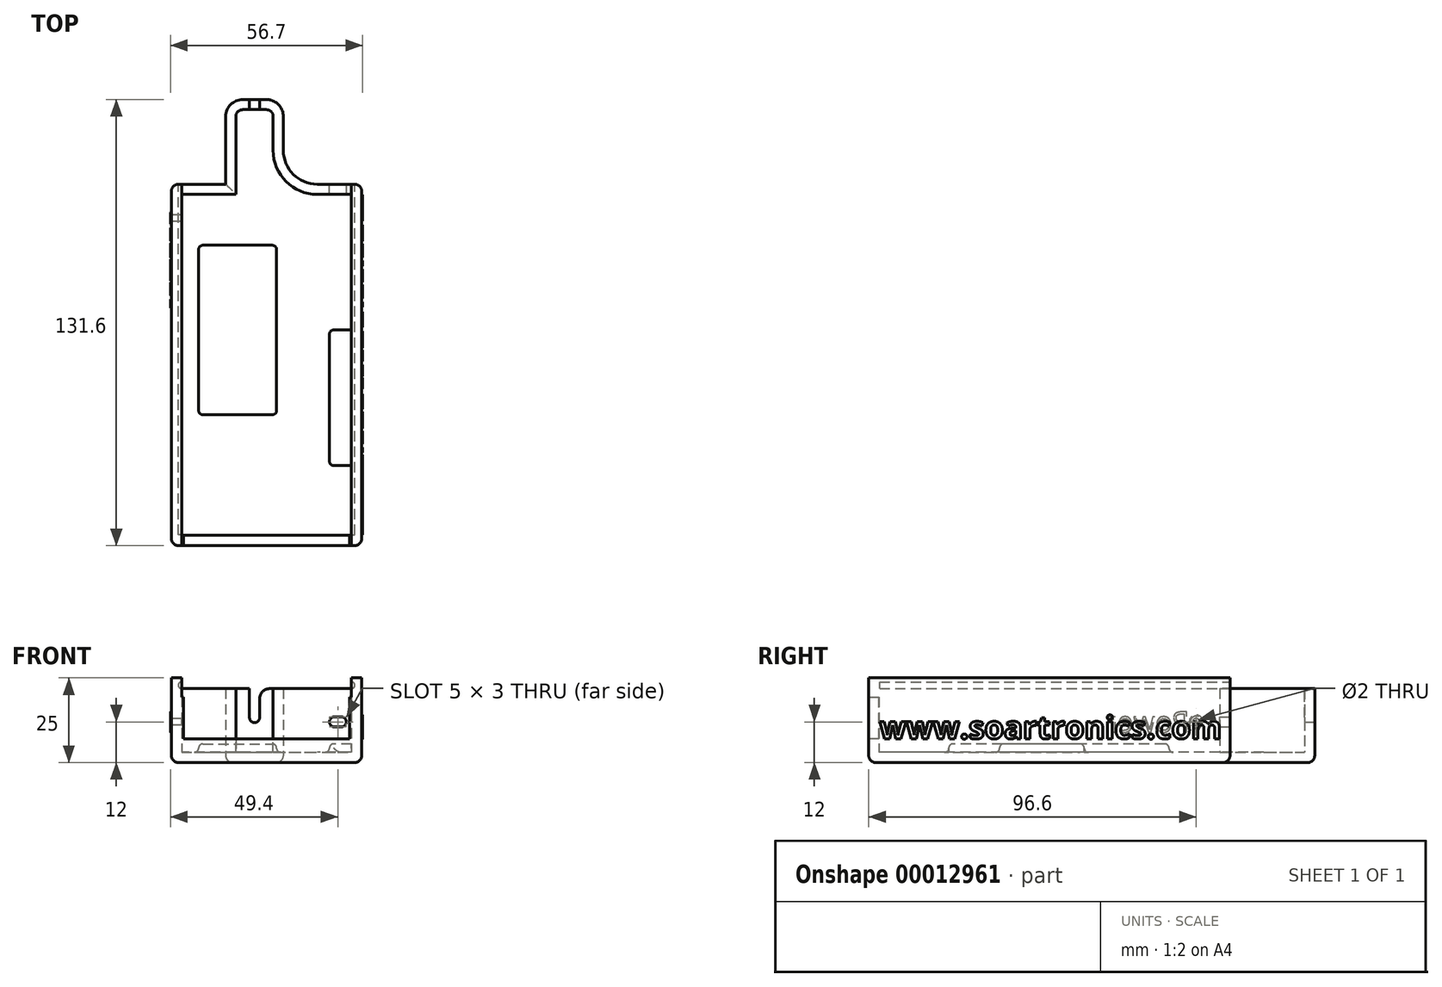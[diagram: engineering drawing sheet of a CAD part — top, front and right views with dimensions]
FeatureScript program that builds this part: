
annotation { "Feature Type Name" : "Feature", "Feature Type Description" : "" }
export const myFeature = defineFeature(function(context is Context, id is Id, definition is map)
    precondition{}
    {
        {
            var Q0;
            Q0=qCreatedBy(makeId("Top.planeOp"),FACE);
            var sketch = newSketch(context, id + "F0", { "sketchPlane" : qUnion([Q0])});
            skLineSegment(sketch, "E0.rect.bottom", {"start": v(28.05, 53.3) * mm, "end": v(-28.05, 53.3) * mm});
            skLineSegment(sketch, "E0.rect.top", {"start": v(28.05, -53.3) * mm, "end": v(-28.05, -53.3) * mm});
            skLineSegment(sketch, "E0.rect.left", {"start": v(28.05, 53.3) * mm, "end": v(28.05, -53.3) * mm});
            skLineSegment(sketch, "E0.rect.right", {"start": v(-28.05, 53.3) * mm, "end": v(-28.05, -53.3) * mm});
            skPoint(sketch, "E0.rect.middle", {"position": v(0, 0) * mm});
            skSolve(sketch);
        }
        {
            var Q0;
            Q0=makeQuery(id+"F0.imprint","IMPRINT",FACE,{"disambiguationData":[TD([[makeQuery(id+"F0.imprint","IMPRINT",EDGE,{"derivedFrom":sQuery(id+"F0.wireOp",EDGE,"E0.rect.bottom")}),1.0]])]});
            extrude(context, id + "F1", {"entities" : qUnion([Q0]), "depth" : 25 * mm});
        }
        {
            var Q0;
            Q0=qCreatedBy(makeId("Top.planeOp"),FACE);
            var sketch = newSketch(context, id + "F2", { "sketchPlane" : qUnion([Q0])});
            skLineSegment(sketch, "E1.bottom", {"start": v(4.95, 53.3) * mm, "end": v(-12.05, 53.3) * mm});
            skLineSegment(sketch, "E1.top", {"start": v(4.95, 78.3) * mm, "end": v(-12.05, 78.3) * mm});
            skLineSegment(sketch, "E1.left", {"start": v(4.95, 53.3) * mm, "end": v(4.95, 78.3) * mm});
            skLineSegment(sketch, "E1.right", {"start": v(-12.05, 53.3) * mm, "end": v(-12.05, 78.3) * mm});
            skSolve(sketch);
        }
        {
            var Q0;
            Q0=makeQuery(id+"F2.imprint","IMPRINT",FACE,{"disambiguationData":[TD([[makeQuery(id+"F2.imprint","IMPRINT",EDGE,{"derivedFrom":sQuery(id+"F2.wireOp",EDGE,"E1.bottom")}),-1.0]])]});
            extrude(context, id + "F3", {"entities" : qUnion([Q0]), "operationType" : NewBodyOperationType.ADD, "depth" : 25 * mm});
        }
        {
            var Q0;
            Q0=makeQuery(id+"F3.opExtrude","SWEPT_EDGE",EDGE,{"disambiguationData":[OSD([sQuery(id+"F2.wireOp",EDGE,"E1.bottom"),sQuery(id+"F2.wireOp",EDGE,"E1.left")])]});
            var Q1;
            Q1=makeQuery(id+"F3.opExtrude","SWEPT_EDGE",EDGE,{"disambiguationData":[OSD([sQuery(id+"F2.wireOp",EDGE,"E1.bottom"),sQuery(id+"F2.wireOp",EDGE,"E1.right")])]});
            fillet(context, id + "F4", {"entities" : qUnion([Q0, Q1]), "radius" : 10 * mm, "tangentPropagation" : true, "allowEdgeOverflow" : false});
        }
        {
            var Q0;
            Q0=makeQuery(id+"F3.opExtrude","SWEPT_EDGE",EDGE,{"disambiguationData":[OSD([sQuery(id+"F2.wireOp",EDGE,"E1.top"),sQuery(id+"F2.wireOp",EDGE,"E1.left")])]});
            var Q1;
            Q1=makeQuery(id+"F3.opExtrude","SWEPT_EDGE",EDGE,{"disambiguationData":[OSD([sQuery(id+"F2.wireOp",EDGE,"E1.top"),sQuery(id+"F2.wireOp",EDGE,"E1.right")])]});
            fillet(context, id + "F5", {"entities" : qUnion([Q0, Q1]), "radius" : 5 * mm, "tangentPropagation" : true, "allowEdgeOverflow" : false});
        }
        {
            var Q0;
            Q0=makeQuery(id+"F3.boolean.opBoolean","MERGE",FACE,{"derivedFrom":[makeQuery(id+"F1.opExtrude","CAP_FACE",FACE,{"disambiguationData":[OSD([sQuery(id+"F0.wireOp",EDGE,"E0.rect.bottom"),sQuery(id+"F0.wireOp",EDGE,"E0.rect.top"),sQuery(id+"F0.wireOp",EDGE,"E0.rect.left"),sQuery(id+"F0.wireOp",EDGE,"E0.rect.right")])],"isStart":false}),makeQuery(id+"F3.opExtrude","CAP_FACE",FACE,{"disambiguationData":[OSD([sQuery(id+"F2.wireOp",EDGE,"E1.bottom"),sQuery(id+"F2.wireOp",EDGE,"E1.top"),sQuery(id+"F2.wireOp",EDGE,"E1.left"),sQuery(id+"F2.wireOp",EDGE,"E1.right")])],"isStart":false})]});
            var Q1;
            Q1=makeQuery(id+"F1.opExtrude","SWEPT_FACE",FACE,{"disambiguationData":[OSD([sQuery(id+"F0.wireOp",EDGE,"E0.rect.top")])]});
            shell(context, id + "F6", {"entities" : qUnion([Q0, Q1]), "thickness" : 3 * mm});
        }
        {
            var Q0;
            Q0=makeQuery(id+"F6.opShell","OFFSET_FACE",FACE,{"disambiguationData":[OSD([sQuery(id+"F0.wireOp",EDGE,"E0.rect.bottom"),sQuery(id+"F0.wireOp",EDGE,"E0.rect.top"),sQuery(id+"F0.wireOp",EDGE,"E0.rect.left"),sQuery(id+"F0.wireOp",EDGE,"E0.rect.right"),sQuery(id+"F2.wireOp",EDGE,"E1.bottom"),sQuery(id+"F2.wireOp",EDGE,"E1.top"),sQuery(id+"F2.wireOp",EDGE,"E1.left"),sQuery(id+"F2.wireOp",EDGE,"E1.right")])]});
            var sketch = newSketch(context, id + "F7", { "sketchPlane" : qUnion([Q0])});
            skLineSegment(sketch, "E2.bottom", {"start": v(-20.05, 35.3) * mm, "end": v(2.95, 35.3) * mm});
            skLineSegment(sketch, "E2.top", {"start": v(-20.05, -14.7) * mm, "end": v(2.95, -14.7) * mm});
            skLineSegment(sketch, "E2.left", {"start": v(-20.05, 35.3) * mm, "end": v(-20.05, -14.7) * mm});
            skLineSegment(sketch, "E2.right", {"start": v(2.95, 35.3) * mm, "end": v(2.95, -14.7) * mm});
            skLineSegment(sketch, "E3.bottom", {"start": v(25.05, -29.7) * mm, "end": v(18.55, -29.7) * mm});
            skLineSegment(sketch, "E3.top", {"start": v(25.05, 10.3) * mm, "end": v(18.55, 10.3) * mm});
            skLineSegment(sketch, "E3.left", {"start": v(25.05, -29.7) * mm, "end": v(25.05, 10.3) * mm});
            skLineSegment(sketch, "E3.right", {"start": v(18.55, -29.7) * mm, "end": v(18.55, 10.3) * mm});
            skSolve(sketch);
        }
        {
            var Q0;
            Q0=makeQuery(id+"F7.imprint","IMPRINT",FACE,{"disambiguationData":[TD([[makeQuery(id+"F7.imprint","IMPRINT",EDGE,{"derivedFrom":sQuery(id+"F7.wireOp",EDGE,"E2.bottom")}),-1.0]])]});
            var Q1;
            Q1=makeQuery(id+"F7.imprint","IMPRINT",FACE,{"disambiguationData":[TD([[makeQuery(id+"F7.imprint","IMPRINT",EDGE,{"derivedFrom":sQuery(id+"F7.wireOp",EDGE,"E3.bottom")}),-1.0]])]});
            extrude(context, id + "F8", {"entities" : qUnion([Q0, Q1]), "operationType" : NewBodyOperationType.ADD, "depth" : 2.5 * mm});
        }
        {
            var Q0;
            Q0=makeQuery(id+"F8.opExtrude","SWEPT_FACE",FACE,{"disambiguationData":[OSD([sQuery(id+"F7.wireOp",EDGE,"E2.top")])]});
            var Q1;
            Q1=makeQuery(id+"F8.opExtrude","SWEPT_FACE",FACE,{"disambiguationData":[OSD([sQuery(id+"F7.wireOp",EDGE,"E2.right")])]});
            var Q2;
            Q2=makeQuery(id+"F8.opExtrude","SWEPT_FACE",FACE,{"disambiguationData":[OSD([sQuery(id+"F7.wireOp",EDGE,"E2.bottom")])]});
            var Q3;
            Q3=makeQuery(id+"F8.opExtrude","SWEPT_FACE",FACE,{"disambiguationData":[OSD([sQuery(id+"F7.wireOp",EDGE,"E2.left")])]});
            var Q4;
            Q4=makeQuery(id+"F8.opExtrude","SWEPT_FACE",FACE,{"disambiguationData":[OSD([sQuery(id+"F7.wireOp",EDGE,"E3.right")])]});
            var Q5;
            Q5=makeQuery(id+"F8.opExtrude","CAP_EDGE",EDGE,{"disambiguationData":[OSD([sQuery(id+"F7.wireOp",EDGE,"E3.bottom")])],"isStart":true});
            var Q6;
            Q6=makeQuery(id+"F8.opExtrude","CAP_EDGE",EDGE,{"disambiguationData":[OSD([sQuery(id+"F7.wireOp",EDGE,"E3.bottom")])],"isStart":false});
            var Q7;
            Q7=makeQuery(id+"F8.opExtrude","CAP_EDGE",EDGE,{"disambiguationData":[OSD([sQuery(id+"F7.wireOp",EDGE,"E3.top")])],"isStart":false});
            fillet(context, id + "F9", {"entities" : qUnion([Q0, Q1, Q2, Q3, Q4, Q5, Q6, Q7]), "radius" : 1.25 * mm, "tangentPropagation" : true, "allowEdgeOverflow" : false});
        }
        {
            var Q0;
            Q0=makeQuery(id+"F3.boolean.opBoolean","MERGE",FACE,{"derivedFrom":[makeQuery(id+"F1.opExtrude","CAP_FACE",FACE,{"disambiguationData":[OSD([sQuery(id+"F0.wireOp",EDGE,"E0.rect.bottom"),sQuery(id+"F0.wireOp",EDGE,"E0.rect.top"),sQuery(id+"F0.wireOp",EDGE,"E0.rect.left"),sQuery(id+"F0.wireOp",EDGE,"E0.rect.right")])],"isStart":false}),makeQuery(id+"F3.opExtrude","CAP_FACE",FACE,{"disambiguationData":[OSD([sQuery(id+"F2.wireOp",EDGE,"E1.bottom"),sQuery(id+"F2.wireOp",EDGE,"E1.top"),sQuery(id+"F2.wireOp",EDGE,"E1.left"),sQuery(id+"F2.wireOp",EDGE,"E1.right")])],"isStart":false})]});
            var sketch = newSketch(context, id + "F10", { "sketchPlane" : qUnion([Q0])});
            skLineSegment(sketch, "E4.bottom", {"start": v(-25.05, 50.3) * mm, "end": v(25.05, 50.3) * mm});
            skLineSegment(sketch, "E4.top", {"start": v(-25.05, 80.3) * mm, "end": v(25.05, 80.3) * mm});
            skLineSegment(sketch, "E4.left", {"start": v(-25.05, 50.3) * mm, "end": v(-25.05, 80.3) * mm});
            skLineSegment(sketch, "E4.right", {"start": v(25.05, 50.3) * mm, "end": v(25.05, 80.3) * mm});
            skSolve(sketch);
        }
        {
            var Q0;
            {var subQ21=sQuery(id+"F10.wireOp",EDGE,"E4.top");Q0=makeQuery(id+"F10.imprint","IMPRINT",FACE,{"disambiguationData":[TD([[makeQuery(id+"F10.imprint","IMPRINT",EDGE,{"derivedFrom":subQ21}),-1.0]])]});}
            var Q1;
            {var subQ2=sQuery(id+"F2.wireOp",EDGE,"E1.top");Q1=makeQuery(id+"F10.imprint","IMPRINT",FACE,{"disambiguationData":[TD([[makeQuery(id+"F10.imprint","IMPRINT",EDGE,{"derivedFrom":makeQuery(id+"F6.opShell","OFFSET_EDGE",EDGE,{"disambiguationData":[OSD([subQ2]),TDD([makeQuery(id+"F3.opExtrude","CAP_EDGE",EDGE,{"disambiguationData":[OSD([subQ2])],"isStart":false})])]})}),1.0]])]});}
            var Q2;
            {var subQ3=sQuery(id+"F2.wireOp",EDGE,"E1.top");var subQ18=makeQuery(id+"F3.opExtrude","CAP_EDGE",EDGE,{"disambiguationData":[OSD([subQ3])],"isStart":false});Q2=makeQuery(id+"F10.imprint","IMPRINT",FACE,{"disambiguationData":[TD([[makeQuery(id+"F10.imprint","IMPRINT",EDGE,{"derivedFrom":subQ18}),1.0]])]});}
            extrude(context, id + "F11", {"entities" : qUnion([Q0, Q1, Q2]), "operationType" : NewBodyOperationType.REMOVE, "oppositeDirection" : true, "depth" : 3.2 * mm});
        }
        {
            var Q0;
            Q0=makeQuery(id+"F6.opShell","OFFSET_FACE",FACE,{"disambiguationData":[OSD([sQuery(id+"F0.wireOp",EDGE,"E0.rect.bottom"),sQuery(id+"F0.wireOp",EDGE,"E0.rect.top"),sQuery(id+"F0.wireOp",EDGE,"E0.rect.left"),sQuery(id+"F0.wireOp",EDGE,"E0.rect.right"),sQuery(id+"F2.wireOp",EDGE,"E1.bottom"),sQuery(id+"F2.wireOp",EDGE,"E1.top"),sQuery(id+"F2.wireOp",EDGE,"E1.left"),sQuery(id+"F2.wireOp",EDGE,"E1.right")])]});
            var sketch = newSketch(context, id + "F12", { "sketchPlane" : qUnion([Q0])});
            skLineSegment(sketch, "E5.bottom", {"start": v(-25.05, -53.3) * mm, "end": v(25.05, -53.3) * mm});
            skLineSegment(sketch, "E5.top", {"start": v(-25.05, -50.3) * mm, "end": v(25.05, -50.3) * mm});
            skLineSegment(sketch, "E5.left", {"start": v(-25.05, -53.3) * mm, "end": v(-25.05, -50.3) * mm});
            skLineSegment(sketch, "E5.right", {"start": v(25.05, -53.3) * mm, "end": v(25.05, -50.3) * mm});
            skSolve(sketch);
        }
        {
            var Q0;
            Q0=makeQuery(id+"F12.imprint","IMPRINT",FACE,{"disambiguationData":[TD([[makeQuery(id+"F12.imprint","IMPRINT",EDGE,{"derivedFrom":sQuery(id+"F12.wireOp",EDGE,"E5.bottom")}),-1.0]])]});
            extrude(context, id + "F13", {"entities" : qUnion([Q0]), "operationType" : NewBodyOperationType.ADD, "depth" : 4 * mm});
        }
        {
            var Q0;
            Q0=makeQuery(id+"F11.boolean.opBoolean","MERGE",FACE,{"derivedFrom":[makeQuery(id+"F6.opShell","OFFSET_FACE",FACE,{"disambiguationData":[OSD([sQuery(id+"F0.wireOp",EDGE,"E0.rect.right")])]}),makeQuery(id+"F11.opExtrude","SWEPT_FACE",FACE,{"disambiguationData":[OSD([sQuery(id+"F10.wireOp",EDGE,"E4.left")])]})]});
            var sketch = newSketch(context, id + "F14", { "sketchPlane" : qUnion([Q0])});
            skLineSegment(sketch, "E6.bottom", {"start": v(-53.3, 7) * mm, "end": v(-50.3, 7) * mm});
            skLineSegment(sketch, "E6.top", {"start": v(-53.3, 19.35) * mm, "end": v(-50.3, 19.35) * mm});
            skLineSegment(sketch, "E6.left", {"start": v(-53.3, 7) * mm, "end": v(-53.3, 19.35) * mm});
            skLineSegment(sketch, "E6.right", {"start": v(-50.3, 7) * mm, "end": v(-50.3, 19.35) * mm});
            skSolve(sketch);
        }
        {
            var Q0;
            Q0=makeQuery(id+"F14.imprint","IMPRINT",FACE,{"disambiguationData":[TD([[makeQuery(id+"F14.imprint","IMPRINT",EDGE,{"derivedFrom":sQuery(id+"F14.wireOp",EDGE,"E6.top")}),-1.0]])]});
            var Q1;
            {var subQ10=sQuery(id+"F14.wireOp",EDGE,"E6.left");Q1=makeQuery(id+"F14.imprint","IMPRINT",FACE,{"disambiguationData":[TD([[makeQuery(id+"F14.imprint","IMPRINT",EDGE,{"derivedFrom":subQ10}),1.0]])]});}
            extrude(context, id + "F15", {"entities" : qUnion([Q0, Q1]), "operationType" : NewBodyOperationType.ADD, "depth" : .5 * mm});
        }
        {
            var Q0;
            Q0=makeQuery(id+"F11.boolean.opBoolean","MERGE",FACE,{"derivedFrom":[makeQuery(id+"F6.opShell","OFFSET_FACE",FACE,{"disambiguationData":[OSD([sQuery(id+"F0.wireOp",EDGE,"E0.rect.left")])]}),makeQuery(id+"F11.opExtrude","SWEPT_FACE",FACE,{"disambiguationData":[OSD([sQuery(id+"F10.wireOp",EDGE,"E4.right")])]})]});
            var sketch = newSketch(context, id + "F16", { "sketchPlane" : qUnion([Q0])});
            skLineSegment(sketch, "E7.bottom", {"start": v(53.3, 7) * mm, "end": v(50.3, 7) * mm});
            skLineSegment(sketch, "E7.top", {"start": v(53.3, 19.35) * mm, "end": v(50.3, 19.35) * mm});
            skLineSegment(sketch, "E7.left", {"start": v(53.3, 7) * mm, "end": v(53.3, 19.35) * mm});
            skLineSegment(sketch, "E7.right", {"start": v(50.3, 7) * mm, "end": v(50.3, 19.35) * mm});
            skSolve(sketch);
        }
        {
            var Q0;
            Q0=makeQuery(id+"F16.imprint","IMPRINT",FACE,{"disambiguationData":[TD([[makeQuery(id+"F16.imprint","IMPRINT",EDGE,{"derivedFrom":sQuery(id+"F16.wireOp",EDGE,"E7.top")}),1.0]])]});
            extrude(context, id + "F17", {"entities" : qUnion([Q0]), "operationType" : NewBodyOperationType.ADD, "depth" : .5 * mm});
        }
        {
            var Q0;
            {var subQ0=sQuery(id+"F0.wireOp",EDGE,"E0.rect.bottom");var subQ5=sQuery(id+"F0.wireOp",EDGE,"E0.rect.left");Q0=makeQuery(id+"F3.boolean.opBoolean","SPLIT",FACE,{"disambiguationData":[TD([makeQuery(id+"F1.opExtrude","SWEPT_FACE",FACE,{"disambiguationData":[OSD([subQ5])]})])],"derivedFrom":makeQuery(id+"F1.opExtrude","SWEPT_FACE",FACE,{"disambiguationData":[OSD([subQ0])]})});}
            var sketch = newSketch(context, id + "F18", { "sketchPlane" : qUnion([Q0])});
            skCircle(sketch, "E8", {"center": v(-25.05, 22.8) * mm, "radius": 1 * mm});
            skCircle(sketch, "E9", {"center": v(25.05, 22.8) * mm, "radius": 1 * mm});
            skSolve(sketch);
        }
        {
            var Q0;
            Q0=makeQuery(id+"F18.imprint","IMPRINT",FACE,{"disambiguationData":[TD([[makeQuery(id+"F18.imprint","IMPRINT",EDGE,{"derivedFrom":sQuery(id+"F18.wireOp",EDGE,"2592f864-b095-4476-8146-10c1a5430829.bottom")}),-1.0]])]});
            var Q1;
            {var subQ0=sQuery(id+"F0.wireOp",EDGE,"E0.rect.bottom");var subQ5=sQuery(id+"F0.wireOp",EDGE,"E0.rect.left");var subQ8=makeQuery(id+"F11.boolean.opBoolean","INTERSECT",EDGE,{"derivedFrom":[makeQuery(id+"F3.boolean.opBoolean","SPLIT",FACE,{"disambiguationData":[TD([makeQuery(id+"F1.opExtrude","SWEPT_FACE",FACE,{"disambiguationData":[OSD([subQ5])]})])],"derivedFrom":makeQuery(id+"F1.opExtrude","SWEPT_FACE",FACE,{"disambiguationData":[OSD([subQ0])]})}),makeQuery(id+"F11.opExtrude","SWEPT_FACE",FACE,{"disambiguationData":[OSD([sQuery(id+"F10.wireOp",EDGE,"E4.right")])]})]});var subQ9=sQuery(id+"F18.wireOp",EDGE,"E8");var subQ11=makeQuery(id+"F18.imprint","INTERSECT",VERTEX,{"disambiguationData":[OD(0.0)],"derivedFrom":[subQ8,subQ9]});Q1=makeQuery(id+"F18.imprint","IMPRINT",FACE,{"disambiguationData":[TD([[makeQuery(id+"F18.imprint","IMPRINT",EDGE,{"disambiguationData":[TD([[subQ11,-1.0]])],"derivedFrom":subQ9}),1.0]])]});}
            var Q2;
            {var subQ0=sQuery(id+"F0.wireOp",EDGE,"E0.rect.bottom");var subQ5=sQuery(id+"F0.wireOp",EDGE,"E0.rect.left");var subQ8=makeQuery(id+"F11.boolean.opBoolean","INTERSECT",EDGE,{"derivedFrom":[makeQuery(id+"F3.boolean.opBoolean","SPLIT",FACE,{"disambiguationData":[TD([makeQuery(id+"F1.opExtrude","SWEPT_FACE",FACE,{"disambiguationData":[OSD([subQ5])]})])],"derivedFrom":makeQuery(id+"F1.opExtrude","SWEPT_FACE",FACE,{"disambiguationData":[OSD([subQ0])]})}),makeQuery(id+"F11.opExtrude","SWEPT_FACE",FACE,{"disambiguationData":[OSD([sQuery(id+"F10.wireOp",EDGE,"E4.right")])]})]});var subQ9=sQuery(id+"F18.wireOp",EDGE,"E8");var subQ11=makeQuery(id+"F18.imprint","INTERSECT",VERTEX,{"disambiguationData":[OD(0.0)],"derivedFrom":[subQ8,subQ9]});Q2=makeQuery(id+"F18.imprint","IMPRINT",FACE,{"disambiguationData":[TD([[makeQuery(id+"F18.imprint","IMPRINT",EDGE,{"disambiguationData":[TD([[subQ11,1.0]])],"derivedFrom":subQ9}),1.0]])]});}
            var Q3;
            Q3=makeQuery(id+"F18.imprint","IMPRINT",FACE,{"disambiguationData":[TD([[makeQuery(id+"F18.imprint","IMPRINT",EDGE,{"derivedFrom":sQuery(id+"F18.wireOp",EDGE,"38d8f2b0-f12b-4a87-90ba-36eebbe7d9a6.bottom")}),1.0]])]});
            var Q4;
            Q4=makeQuery(id+"F18.imprint","IMPRINT",FACE,{"disambiguationData":[TD([[makeQuery(id+"F18.imprint","IMPRINT",EDGE,{"derivedFrom":sQuery(id+"F18.wireOp",EDGE,"E9")}),1.0]])]});
            extrude(context, id + "F19", {"entities" : qUnion([Q0, Q1, Q2, Q3, Q4]), "operationType" : NewBodyOperationType.REMOVE, "oppositeDirection" : true, "depth" : 103.4 * mm});
        }
        {
            var Q0;
            Q0=makeQuery(id+"F11.boolean.opBoolean","COPY",FACE,{"derivedFrom":makeQuery(id+"F11.opExtrude","CAP_FACE",FACE,{"disambiguationData":[OSD([sQuery(id+"F10.wireOp",EDGE,"E4.bottom"),sQuery(id+"F10.wireOp",EDGE,"E4.top"),sQuery(id+"F10.wireOp",EDGE,"E4.left"),sQuery(id+"F10.wireOp",EDGE,"E4.right")])],"isStart":false})});
            var sketch = newSketch(context, id + "F20", { "sketchPlane" : qUnion([Q0])});
            skLineSegment(sketch, "E10.bottom", {"start": v(-5.05, 78.3) * mm, "end": v(-2.05, 78.3) * mm});
            skLineSegment(sketch, "E10.top", {"start": v(-5.05, 75.3) * mm, "end": v(-2.05, 75.3) * mm});
            skLineSegment(sketch, "E10.left", {"start": v(-5.05, 78.3) * mm, "end": v(-5.05, 75.3) * mm});
            skLineSegment(sketch, "E10.right", {"start": v(-2.05, 78.3) * mm, "end": v(-2.05, 75.3) * mm});
            skSolve(sketch);
        }
        {
            var Q0;
            Q0=makeQuery(id+"F20.imprint","IMPRINT",FACE,{"disambiguationData":[TD([[makeQuery(id+"F20.imprint","IMPRINT",EDGE,{"derivedFrom":sQuery(id+"F20.wireOp",EDGE,"E10.bottom")}),1.0]])]});
            extrude(context, id + "F21", {"entities" : qUnion([Q0]), "operationType" : NewBodyOperationType.REMOVE, "oppositeDirection" : true, "depth" : 10 * mm});
        }
        {
            var Q0;
            Q0=makeQuery(id+"F21.boolean.opBoolean","COPY",EDGE,{"derivedFrom":makeQuery(id+"F21.opExtrude","CAP_EDGE",EDGE,{"disambiguationData":[OSD([sQuery(id+"F20.wireOp",EDGE,"E10.left")])],"isStart":false})});
            var Q1;
            Q1=makeQuery(id+"F21.boolean.opBoolean","COPY",EDGE,{"derivedFrom":makeQuery(id+"F21.opExtrude","CAP_EDGE",EDGE,{"disambiguationData":[OSD([sQuery(id+"F20.wireOp",EDGE,"E10.right")])],"isStart":false})});
            fillet(context, id + "F22", {"entities" : qUnion([Q0, Q1]), "radius" : 1.5 * mm, "tangentPropagation" : true, "allowEdgeOverflow" : false});
        }
        {
            var Q0;
            Q0=makeQuery(id+"F21.boolean.opBoolean","COPY",EDGE,{"derivedFrom":makeQuery(id+"F21.opExtrude","CAP_EDGE",EDGE,{"disambiguationData":[OSD([sQuery(id+"F20.wireOp",EDGE,"E10.right")])],"isStart":true})});
            var Q1;
            Q1=makeQuery(id+"F21.boolean.opBoolean","COPY",EDGE,{"derivedFrom":makeQuery(id+"F21.opExtrude","CAP_EDGE",EDGE,{"disambiguationData":[OSD([sQuery(id+"F20.wireOp",EDGE,"E10.left")])],"isStart":true})});
            fillet(context, id + "F23", {"entities" : qUnion([Q0, Q1]), "radius" : 3 * mm, "tangentPropagation" : true, "allowEdgeOverflow" : false});
        }
        {
            var Q0;
            Q0=makeQuery(id+"F3.boolean.opBoolean","MERGE",FACE,{"derivedFrom":[makeQuery(id+"F1.opExtrude","CAP_FACE",FACE,{"disambiguationData":[OSD([sQuery(id+"F0.wireOp",EDGE,"E0.rect.bottom"),sQuery(id+"F0.wireOp",EDGE,"E0.rect.top"),sQuery(id+"F0.wireOp",EDGE,"E0.rect.left"),sQuery(id+"F0.wireOp",EDGE,"E0.rect.right")])],"isStart":true}),makeQuery(id+"F3.opExtrude","CAP_FACE",FACE,{"disambiguationData":[OSD([sQuery(id+"F2.wireOp",EDGE,"E1.bottom"),sQuery(id+"F2.wireOp",EDGE,"E1.top"),sQuery(id+"F2.wireOp",EDGE,"E1.left"),sQuery(id+"F2.wireOp",EDGE,"E1.right")])],"isStart":true})]});
            var Q1;
            Q1=makeQuery(id+"F1.opExtrude","SWEPT_EDGE",EDGE,{"disambiguationData":[OSD([sQuery(id+"F0.wireOp",EDGE,"E0.rect.bottom"),sQuery(id+"F0.wireOp",EDGE,"E0.rect.left")])]});
            var Q2;
            Q2=makeQuery(id+"F1.opExtrude","SWEPT_EDGE",EDGE,{"disambiguationData":[OSD([sQuery(id+"F0.wireOp",EDGE,"E0.rect.bottom"),sQuery(id+"F0.wireOp",EDGE,"E0.rect.right")])]});
            var Q3;
            Q3=makeQuery(id+"F1.opExtrude","SWEPT_EDGE",EDGE,{"disambiguationData":[OSD([sQuery(id+"F0.wireOp",EDGE,"E0.rect.top"),sQuery(id+"F0.wireOp",EDGE,"E0.rect.left")])]});
            var Q4;
            Q4=makeQuery(id+"F1.opExtrude","SWEPT_EDGE",EDGE,{"disambiguationData":[OSD([sQuery(id+"F0.wireOp",EDGE,"E0.rect.top"),sQuery(id+"F0.wireOp",EDGE,"E0.rect.right")])]});
            fillet(context, id + "F24", {"entities" : qUnion([Q0, Q1, Q2, Q3, Q4]), "radius" : 2 * mm, "tangentPropagation" : true, "allowEdgeOverflow" : false});
        }
        {
            var Q0;
            Q0=makeQuery(id+"F1.opExtrude","SWEPT_FACE",FACE,{"disambiguationData":[OSD([sQuery(id+"F0.wireOp",EDGE,"E0.rect.left")])]});
            var sketch = newSketch(context, id + "F25", { "sketchPlane" : qUnion([Q0])});
            skText(sketch, "E11", { "text": "www.soartronics.com", "fontName": "OpenSans-Bold.ttf"});
            const initialGuessF25  = {"E11": [-0.0502, 0.00702, 1, 0, 0.00667]};
            skSetInitialGuess(sketch, initialGuessF25);
            skSolve(sketch);
        }
        {
            var Q0;
            Q0=makeQuery(id+"F25.imprint","IMPRINT",FACE,{"disambiguationData":[TD([[makeQuery(id+"F25.imprint","IMPRINT",EDGE,{"derivedFrom":sQuery(id+"F25.wireOp",EDGE,"E11.sketch_text.stroke-0")}),-1.0]])]});
            var Q1;
            Q1=makeQuery(id+"F25.imprint","IMPRINT",FACE,{"disambiguationData":[TD([[makeQuery(id+"F25.imprint","IMPRINT",EDGE,{"derivedFrom":sQuery(id+"F25.wireOp",EDGE,"E11.sketch_text.stroke-26")}),-1.0]])]});
            var Q2;
            Q2=makeQuery(id+"F25.imprint","IMPRINT",FACE,{"disambiguationData":[TD([[makeQuery(id+"F25.imprint","IMPRINT",EDGE,{"derivedFrom":sQuery(id+"F25.wireOp",EDGE,"E11.sketch_text.stroke-52")}),-1.0]])]});
            var Q3;
            Q3=makeQuery(id+"F25.imprint","IMPRINT",FACE,{"disambiguationData":[TD([[makeQuery(id+"F25.imprint","IMPRINT",EDGE,{"derivedFrom":sQuery(id+"F25.wireOp",EDGE,"E11.sketch_text.stroke-86")}),-1.0]])]});
            var Q4;
            Q4=makeQuery(id+"F25.imprint","IMPRINT",FACE,{"disambiguationData":[TD([[makeQuery(id+"F25.imprint","IMPRINT",EDGE,{"derivedFrom":sQuery(id+"F25.wireOp",EDGE,"E11.sketch_text.stroke-78")}),-1.0]])]});
            var Q5;
            Q5=makeQuery(id+"F25.imprint","IMPRINT",FACE,{"disambiguationData":[TD([[makeQuery(id+"F25.imprint","IMPRINT",EDGE,{"derivedFrom":sQuery(id+"F25.wireOp",EDGE,"E11.sketch_text.stroke-112")}),-1.0]])]});
            var Q6;
            Q6=makeQuery(id+"F25.imprint","IMPRINT",FACE,{"disambiguationData":[TD([[makeQuery(id+"F25.imprint","IMPRINT",EDGE,{"derivedFrom":sQuery(id+"F25.wireOp",EDGE,"E11.sketch_text.stroke-130")}),-1.0]])]});
            var Q7;
            Q7=makeQuery(id+"F25.imprint","IMPRINT",FACE,{"disambiguationData":[TD([[makeQuery(id+"F25.imprint","IMPRINT",EDGE,{"derivedFrom":sQuery(id+"F25.wireOp",EDGE,"E11.sketch_text.stroke-155")}),-1.0]])]});
            var Q8;
            Q8=makeQuery(id+"F25.imprint","IMPRINT",FACE,{"disambiguationData":[TD([[makeQuery(id+"F25.imprint","IMPRINT",EDGE,{"derivedFrom":sQuery(id+"F25.wireOp",EDGE,"E11.sketch_text.stroke-168")}),-1.0]])]});
            var Q9;
            Q9=makeQuery(id+"F25.imprint","IMPRINT",FACE,{"disambiguationData":[TD([[makeQuery(id+"F25.imprint","IMPRINT",EDGE,{"derivedFrom":sQuery(id+"F25.wireOp",EDGE,"E11.sketch_text.stroke-186")}),-1.0]])]});
            var Q10;
            Q10=makeQuery(id+"F25.imprint","IMPRINT",FACE,{"disambiguationData":[TD([[makeQuery(id+"F25.imprint","IMPRINT",EDGE,{"derivedFrom":sQuery(id+"F25.wireOp",EDGE,"E11.sketch_text.stroke-199")}),-1.0]])]});
            var Q11;
            Q11=makeQuery(id+"F25.imprint","IMPRINT",FACE,{"disambiguationData":[TD([[makeQuery(id+"F25.imprint","IMPRINT",EDGE,{"derivedFrom":sQuery(id+"F25.wireOp",EDGE,"E11.sketch_text.stroke-217")}),-1.0]])]});
            var Q12;
            Q12=makeQuery(id+"F25.imprint","IMPRINT",FACE,{"disambiguationData":[TD([[makeQuery(id+"F25.imprint","IMPRINT",EDGE,{"derivedFrom":sQuery(id+"F25.wireOp",EDGE,"E11.sketch_text.stroke-239")}),-1.0]])]});
            var Q13;
            Q13=makeQuery(id+"F25.imprint","IMPRINT",FACE,{"disambiguationData":[TD([[makeQuery(id+"F25.imprint","IMPRINT",EDGE,{"derivedFrom":sQuery(id+"F25.wireOp",EDGE,"E11.sketch_text.stroke-234")}),-1.0]])]});
            var Q14;
            Q14=makeQuery(id+"F25.imprint","IMPRINT",FACE,{"disambiguationData":[TD([[makeQuery(id+"F25.imprint","IMPRINT",EDGE,{"derivedFrom":sQuery(id+"F25.wireOp",EDGE,"E11.sketch_text.stroke-257")}),-1.0]])]});
            var Q15;
            Q15=makeQuery(id+"F25.imprint","IMPRINT",FACE,{"disambiguationData":[TD([[makeQuery(id+"F25.imprint","IMPRINT",EDGE,{"derivedFrom":sQuery(id+"F25.wireOp",EDGE,"E11.sketch_text.stroke-283")}),-1.0]])]});
            var Q16;
            Q16=makeQuery(id+"F25.imprint","IMPRINT",FACE,{"disambiguationData":[TD([[makeQuery(id+"F25.imprint","IMPRINT",EDGE,{"derivedFrom":sQuery(id+"F25.wireOp",EDGE,"E11.sketch_text.stroke-291")}),-1.0]])]});
            var Q17;
            Q17=makeQuery(id+"F25.imprint","IMPRINT",FACE,{"disambiguationData":[TD([[makeQuery(id+"F25.imprint","IMPRINT",EDGE,{"derivedFrom":sQuery(id+"F25.wireOp",EDGE,"E11.sketch_text.stroke-305")}),-1.0]])]});
            var Q18;
            Q18=makeQuery(id+"F25.imprint","IMPRINT",FACE,{"disambiguationData":[TD([[makeQuery(id+"F25.imprint","IMPRINT",EDGE,{"derivedFrom":sQuery(id+"F25.wireOp",EDGE,"E11.sketch_text.stroke-323")}),-1.0]])]});
            var Q19;
            Q19=makeQuery(id+"F25.imprint","IMPRINT",FACE,{"disambiguationData":[TD([[makeQuery(id+"F25.imprint","IMPRINT",EDGE,{"derivedFrom":sQuery(id+"F25.wireOp",EDGE,"E11.sketch_text.stroke-243")}),-1.0]])]});
            extrude(context, id + "F26", {"entities" : qUnion([Q0, Q1, Q2, Q3, Q4, Q5, Q6, Q7, Q8, Q9, Q10, Q11, Q12, Q13, Q14, Q15, Q16, Q17, Q18, Q19]), "operationType" : NewBodyOperationType.ADD, "depth" : .3 * mm});
        }
        {
            var Q0;
            {var subQ0=sQuery(id+"F0.wireOp",EDGE,"E0.rect.bottom");var subQ5=sQuery(id+"F0.wireOp",EDGE,"E0.rect.left");Q0=makeQuery(id+"F24.opFillet","SPLIT",FACE,{"disambiguationData":[OD(0.0)],"derivedFrom":makeQuery(id+"F3.boolean.opBoolean","SPLIT",FACE,{"disambiguationData":[TD([makeQuery(id+"F1.opExtrude","SWEPT_FACE",FACE,{"disambiguationData":[OSD([subQ5])]})])],"derivedFrom":makeQuery(id+"F1.opExtrude","SWEPT_FACE",FACE,{"disambiguationData":[OSD([subQ0])]})})});}
            var sketch = newSketch(context, id + "F27", { "sketchPlane" : qUnion([Q0])});
            skArc(sketch, "E12", {"start": v(-22.05, 13.5) * mm, "mid": v(-23.55, 12) * mm, "end": v(-22.05, 10.5) * mm});
            skArc(sketch, "E13", {"start": v(-20.05, 10.5) * mm, "mid": v(-18.55, 12) * mm, "end": v(-20.05, 13.5) * mm});
            skLineSegment(sketch, "E14", {"start": v(-22.05, 13.5) * mm, "end": v(-20.05, 13.5) * mm});
            skLineSegment(sketch, "E15", {"start": v(-22.05, 10.5) * mm, "end": v(-20.05, 10.5) * mm});
            skSolve(sketch);
        }
        {
            var Q0;
            Q0=makeQuery(id+"F27.imprint","IMPRINT",FACE,{"disambiguationData":[TD([[makeQuery(id+"F27.imprint","IMPRINT",EDGE,{"derivedFrom":sQuery(id+"F27.wireOp",EDGE,"E12")}),1.0]])]});
            extrude(context, id + "F28", {"entities" : qUnion([Q0]), "operationType" : NewBodyOperationType.REMOVE, "endBound" : BoundingType.UP_TO_NEXT, "oppositeDirection" : true, "depth" : 3.67 * mm});
        }
        {
            var Q0;
            Q0=makeQuery(id+"F1.opExtrude","SWEPT_FACE",FACE,{"disambiguationData":[OSD([sQuery(id+"F0.wireOp",EDGE,"E0.rect.right")])]});
            var sketch = newSketch(context, id + "F29", { "sketchPlane" : qUnion([Q0])});
            skCircle(sketch, "E16", {"center": v(-43.3, 12) * mm, "radius": 1 * mm});
            skSolve(sketch);
        }
        {
            var Q0;
            Q0=makeQuery(id+"F29.imprint","IMPRINT",FACE,{"disambiguationData":[TD([[makeQuery(id+"F29.imprint","IMPRINT",EDGE,{"derivedFrom":sQuery(id+"F29.wireOp",EDGE,"E16")}),1.0]])]});
            extrude(context, id + "F30", {"entities" : qUnion([Q0]), "operationType" : NewBodyOperationType.REMOVE, "endBound" : BoundingType.UP_TO_NEXT, "oppositeDirection" : true, "depth" : 25 * mm});
        }
        {
            var Q0;
            Q0=makeQuery(id+"F1.opExtrude","SWEPT_FACE",FACE,{"disambiguationData":[OSD([sQuery(id+"F0.wireOp",EDGE,"E0.rect.right")])]});
            var sketch = newSketch(context, id + "F31", { "sketchPlane" : qUnion([Q0])});
            skText(sketch, "E17", { "text": "Power", "fontName": "OpenSans-Regular.ttf"});
            skCircle(sketch, "E18.0", {"center": v(-43.3, 12) * mm, "radius": 1 * mm});
            skPoint(sketch, "E19", {"position": v(-41.3, 12) * mm});
            skCircle(sketch, "E20", {"center": v(-43.3, 12) * mm, "radius": 2 * mm});
            const initialGuessF31  = {"E17": [-0.0413, 0.009, 1, 0, 0.006]};
            skSetInitialGuess(sketch, initialGuessF31);
            skSolve(sketch);
        }
        {
            var Q0;
            Q0=makeQuery(id+"F31.imprint","IMPRINT",FACE,{"disambiguationData":[TD([[makeQuery(id+"F31.imprint","IMPRINT",EDGE,{"derivedFrom":sQuery(id+"F31.wireOp",EDGE,"E17.sketch_text.stroke-0")}),-1.0]])]});
            var Q1;
            Q1=makeQuery(id+"F31.imprint","IMPRINT",FACE,{"disambiguationData":[TD([[makeQuery(id+"F31.imprint","IMPRINT",EDGE,{"derivedFrom":sQuery(id+"F31.wireOp",EDGE,"E17.sketch_text.stroke-15")}),-1.0]])]});
            var Q2;
            Q2=makeQuery(id+"F31.imprint","IMPRINT",FACE,{"disambiguationData":[TD([[makeQuery(id+"F31.imprint","IMPRINT",EDGE,{"derivedFrom":sQuery(id+"F31.wireOp",EDGE,"E17.sketch_text.stroke-32")}),-1.0]])]});
            var Q3;
            Q3=makeQuery(id+"F31.imprint","IMPRINT",FACE,{"disambiguationData":[TD([[makeQuery(id+"F31.imprint","IMPRINT",EDGE,{"derivedFrom":sQuery(id+"F31.wireOp",EDGE,"E17.sketch_text.stroke-55")}),-1.0]])]});
            var Q4;
            Q4=makeQuery(id+"F31.imprint","IMPRINT",FACE,{"disambiguationData":[TD([[makeQuery(id+"F31.imprint","IMPRINT",EDGE,{"derivedFrom":sQuery(id+"F31.wireOp",EDGE,"E17.sketch_text.stroke-74")}),-1.0]])]});
            var Q5;
            Q5=makeQuery(id+"F31.imprint","IMPRINT",FACE,{"disambiguationData":[TD([[makeQuery(id+"F31.imprint","IMPRINT",EDGE,{"derivedFrom":sQuery(id+"F31.wireOp",EDGE,"E18.0")}),-1.0]])]});
            extrude(context, id + "F32", {"entities" : qUnion([Q0, Q1, Q2, Q3, Q4, Q5]), "operationType" : NewBodyOperationType.ADD, "depth" : .3 * mm});
        }
        {
            var Q0;
            Q0=makeQuery(id+"F32.opExtrude","CAP_EDGE",EDGE,{"disambiguationData":[OSD([sQuery(id+"F31.wireOp",EDGE,"E20")])],"isStart":false});
            chamfer(context, id + "F33", {"entities" : qUnion([Q0]), "width" : .3 * mm, "tangentPropagation" : true});
        }
    });
